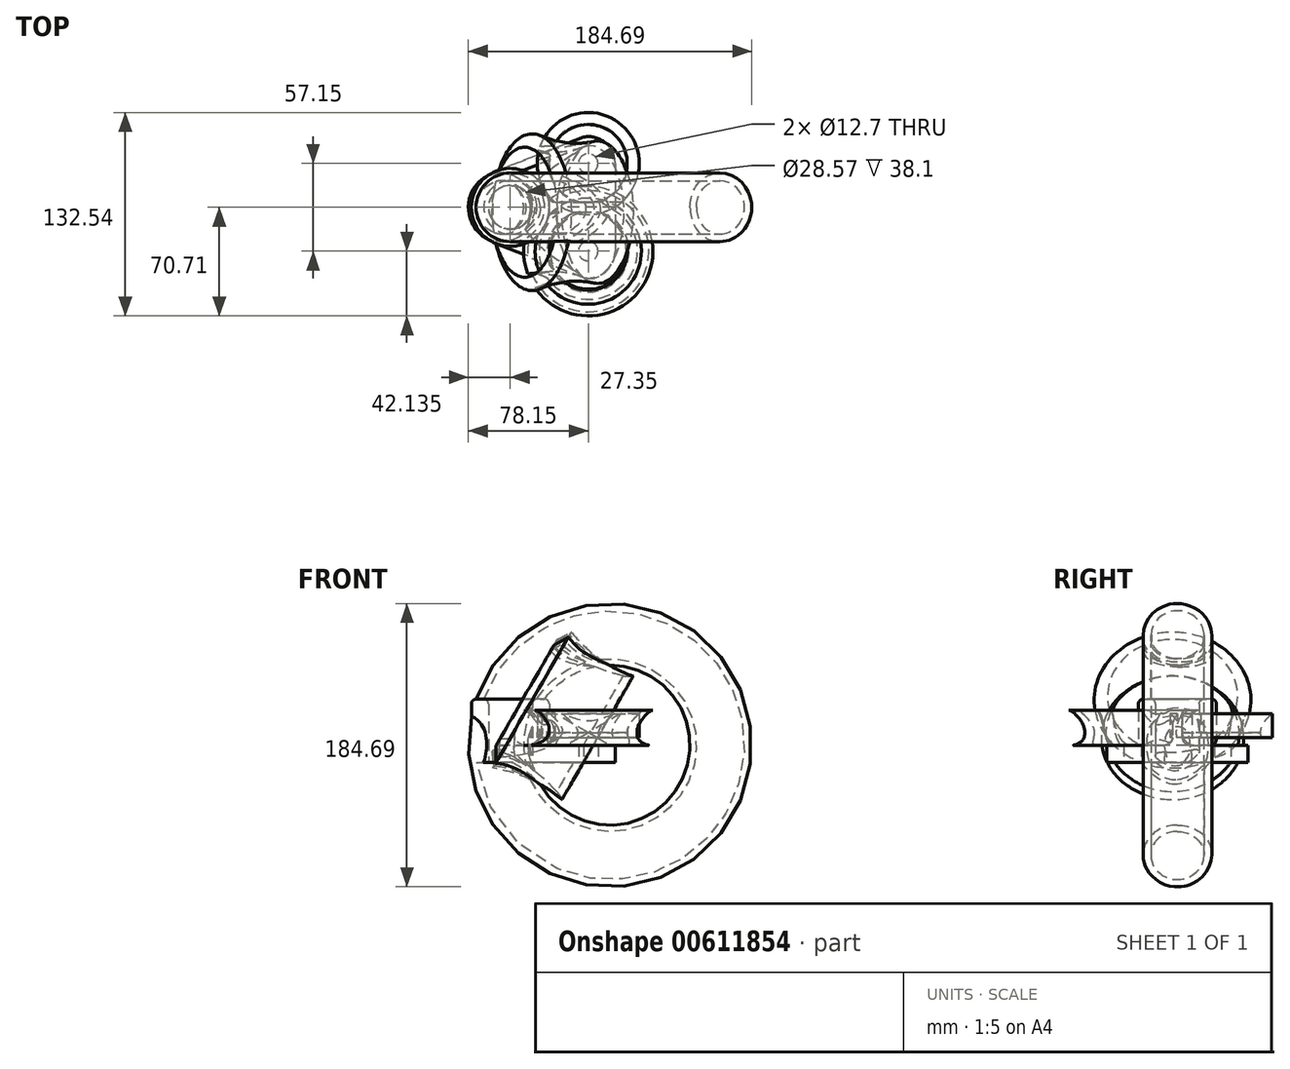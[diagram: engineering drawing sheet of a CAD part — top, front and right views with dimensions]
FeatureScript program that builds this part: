
annotation { "Feature Type Name" : "Feature", "Feature Type Description" : "" }
export const myFeature = defineFeature(function(context is Context, id is Id, definition is map)
    precondition{}
    {
        {
            var Q0;
            Q0=qCreatedBy(makeId("Top.planeOp"),FACE);
            var sketch = newSketch(context, id + "F0", { "sketchPlane" : qUnion([Q0])});
            skCircle(sketch, "E0", {"center": v(0, 0) * mm, "radius": 14.29 * mm});
            skCircle(sketch, "E1", {"center": v(0, 0) * mm, "radius": 25.4 * mm});
            skCircle(sketch, "E2", {"center": v(50.8, 28.57) * mm, "radius": 6.35 * mm});
            skCircle(sketch, "E3", {"center": v(50.8, -28.58) * mm, "radius": 6.35 * mm});
            skArc(sketch, "E4", {"start": v(47.66, 45.81) * mm, "mid": v(62.02, 42.03) * mm, "end": v(68.32, 28.57) * mm});
            skLineSegment(sketch, "E5", {"start": v(47.66, 45.81) * mm, "end": v(-9.22, 23.67) * mm});
            skLineSegment(sketch, "E6", {"start": v(68.32, 28.57) * mm, "end": v(68.32, 0) * mm});
            skLineSegment(sketch, "E7.MirrorCS", {"start": v(68.32, -28.57) * mm, "end": v(68.32, 0) * mm});
            skArc(sketch, "E8.MirrorCS", {"start": v(47.66, -45.81) * mm, "mid": v(62.02, -42.03) * mm, "end": v(68.32, -28.57) * mm});
            skLineSegment(sketch, "E9.MirrorCS", {"start": v(47.66, -45.81) * mm, "end": v(-9.22, -23.67) * mm});
            skSolve(sketch);
        }
        {
            var Q0;
            Q0=makeQuery(id+"F0.imprint","IMPRINT",FACE,{"disambiguationData":[TD([[makeQuery(id+"F0.imprint","IMPRINT",EDGE,{"derivedFrom":sQuery(id+"F0.wireOp",EDGE,"E0")}),-1.0]])]});
            extrude(context, id + "F1", {"entities" : qUnion([Q0]), "depth" : 41.15 * mm, "offsetDistance" : 25.4 * mm});
        }
        {
            var Q0;
            Q0=makeQuery(id+"F0.imprint","IMPRINT",FACE,{"disambiguationData":[TD([[makeQuery(id+"F0.imprint","IMPRINT",EDGE,{"derivedFrom":sQuery(id+"F0.wireOp",EDGE,"E2")}),-1.0]])]});
            extrude(context, id + "F2", {"entities" : qUnion([Q0]), "operationType" : NewBodyOperationType.ADD, "depth" : 11.18 * mm, "offsetDistance" : 25.4 * mm});
        }
        {
            var Q0;
            Q0=qCreatedBy(makeId("Front.planeOp"),FACE);
            var sketch = newSketch(context, id + "F3", { "sketchPlane" : qUnion([Q0])});
            skLineSegment(sketch, "E10", {"start": v(25.4, 11.16) * mm, "end": v(65.02, 11.16) * mm});
            skLineSegment(sketch, "E11", {"start": v(65.02, 11.16) * mm, "end": v(25.4, 34.04) * mm});
            skPoint(sketch, "E12.orphan", {"position": v(25.4, 41.15) * mm});
            skLineSegment(sketch, "E13", {"start": v(25.4, 11.16) * mm, "end": v(19.95, 11.16) * mm});
            skLineSegment(sketch, "E14", {"start": v(19.95, 11.16) * mm, "end": v(19.95, 35.74) * mm});
            skLineSegment(sketch, "E15", {"start": v(19.95, 35.74) * mm, "end": v(25.4, 34.04) * mm});
            skSolve(sketch);
        }
        {
            var Q0;
            Q0=makeQuery(id+"F3.imprint","IMPRINT",FACE,{"disambiguationData":[TD([[makeQuery(id+"F3.imprint","IMPRINT",EDGE,{"derivedFrom":sQuery(id+"F3.wireOp",EDGE,"E10")}),1.0]])]});
            extrude(context, id + "F4", {"entities" : qUnion([Q0]), "operationType" : NewBodyOperationType.ADD, "endBound" : BoundingType.SYMMETRIC, "depth" : 6.35 * mm, "offsetDistance" : 25.4 * mm});
        }
        {
            var Q0;
            Q0=makeQuery(id+"F1.opExtrude","CAP_EDGE",EDGE,{"disambiguationData":[OSD([sQuery(id+"F0.wireOp",EDGE,"E1")])],"isStart":false});
            var Q1;
            Q1=makeQuery(id+"F1.opExtrude","CAP_EDGE",EDGE,{"disambiguationData":[OSD([sQuery(id+"F0.wireOp",EDGE,"E0")])],"isStart":false});
            fillet(context, id + "F5", {"entities" : qUnion([Q0, Q1]), "radius" : 3.05 * mm, "tangentPropagation" : true, "allowEdgeOverflow" : false});
        }
        {
            var Q0;
            {var subQ0=sQuery(id+"F0.wireOp",EDGE,"E1");var subQ1=sQuery(id+"F0.wireOp",EDGE,"E9.MirrorCS");Q0=makeQuery(id+"F4.boolean.opBoolean","SPLIT",EDGE,{"disambiguationData":[TD([makeQuery(id+"F2.opExtrude","SWEPT_FACE",FACE,{"disambiguationData":[OSD([subQ1])]})])],"derivedFrom":makeQuery(id+"F2.opExtrude","CAP_EDGE",EDGE,{"disambiguationData":[OSD([subQ0])],"isStart":false})});}
            var Q1;
            {var subQ0=sQuery(id+"F0.wireOp",EDGE,"E1");var subQ1=sQuery(id+"F0.wireOp",EDGE,"E5");Q1=makeQuery(id+"F4.boolean.opBoolean","SPLIT",EDGE,{"disambiguationData":[TD([makeQuery(id+"F2.opExtrude","SWEPT_FACE",FACE,{"disambiguationData":[OSD([subQ1])]})])],"derivedFrom":makeQuery(id+"F2.opExtrude","CAP_EDGE",EDGE,{"disambiguationData":[OSD([subQ0])],"isStart":false})});}
            var Q2;
            Q2=makeQuery(id+"F4.boolean.opBoolean","INTERSECT",EDGE,{"derivedFrom":[makeQuery(id+"F1.opExtrude","SWEPT_FACE",FACE,{"disambiguationData":[OSD([sQuery(id+"F0.wireOp",EDGE,"E1")])]}),makeQuery(id+"F4.opExtrude","CAP_FACE",FACE,{"disambiguationData":[OSD([sQuery(id+"F3.wireOp",EDGE,"E10"),sQuery(id+"F3.wireOp",EDGE,"E11"),sQuery(id+"F3.wireOp",EDGE,"E13"),sQuery(id+"F3.wireOp",EDGE,"E14"),sQuery(id+"F3.wireOp",EDGE,"E15")])],"isStart":false})]});
            var Q3;
            Q3=makeQuery(id+"F4.boolean.opBoolean","INTERSECT",EDGE,{"derivedFrom":[makeQuery(id+"F2.opExtrude","CAP_FACE",FACE,{"disambiguationData":[OSD([sQuery(id+"F0.wireOp",EDGE,"E1"),sQuery(id+"F0.wireOp",EDGE,"E2"),sQuery(id+"F0.wireOp",EDGE,"E3"),sQuery(id+"F0.wireOp",EDGE,"E4"),sQuery(id+"F0.wireOp",EDGE,"E5"),sQuery(id+"F0.wireOp",EDGE,"E6"),sQuery(id+"F0.wireOp",EDGE,"E7.MirrorCS"),sQuery(id+"F0.wireOp",EDGE,"E8.MirrorCS"),sQuery(id+"F0.wireOp",EDGE,"E9.MirrorCS")])],"isStart":false}),makeQuery(id+"F4.opExtrude","CAP_FACE",FACE,{"disambiguationData":[OSD([sQuery(id+"F3.wireOp",EDGE,"E10"),sQuery(id+"F3.wireOp",EDGE,"E11"),sQuery(id+"F3.wireOp",EDGE,"E13"),sQuery(id+"F3.wireOp",EDGE,"E14"),sQuery(id+"F3.wireOp",EDGE,"E15")])],"isStart":false})]});
            var Q4;
            Q4=makeQuery(id+"F4.boolean.opBoolean","INTERSECT",EDGE,{"derivedFrom":[makeQuery(id+"F2.opExtrude","CAP_FACE",FACE,{"disambiguationData":[OSD([sQuery(id+"F0.wireOp",EDGE,"E1"),sQuery(id+"F0.wireOp",EDGE,"E2"),sQuery(id+"F0.wireOp",EDGE,"E3"),sQuery(id+"F0.wireOp",EDGE,"E4"),sQuery(id+"F0.wireOp",EDGE,"E5"),sQuery(id+"F0.wireOp",EDGE,"E6"),sQuery(id+"F0.wireOp",EDGE,"E7.MirrorCS"),sQuery(id+"F0.wireOp",EDGE,"E8.MirrorCS"),sQuery(id+"F0.wireOp",EDGE,"E9.MirrorCS")])],"isStart":false}),makeQuery(id+"F4.opExtrude","CAP_FACE",FACE,{"disambiguationData":[OSD([sQuery(id+"F3.wireOp",EDGE,"E10"),sQuery(id+"F3.wireOp",EDGE,"E11"),sQuery(id+"F3.wireOp",EDGE,"E13"),sQuery(id+"F3.wireOp",EDGE,"E14"),sQuery(id+"F3.wireOp",EDGE,"E15")])],"isStart":true})]});
            var Q5;
            Q5=makeQuery(id+"F4.boolean.opBoolean","INTERSECT",EDGE,{"derivedFrom":[makeQuery(id+"F1.opExtrude","SWEPT_FACE",FACE,{"disambiguationData":[OSD([sQuery(id+"F0.wireOp",EDGE,"E1")])]}),makeQuery(id+"F4.opExtrude","CAP_FACE",FACE,{"disambiguationData":[OSD([sQuery(id+"F3.wireOp",EDGE,"E10"),sQuery(id+"F3.wireOp",EDGE,"E11"),sQuery(id+"F3.wireOp",EDGE,"E13"),sQuery(id+"F3.wireOp",EDGE,"E14"),sQuery(id+"F3.wireOp",EDGE,"E15")])],"isStart":true})]});
            fillet(context, id + "F6", {"entities" : qUnion([Q0, Q1, Q2, Q3, Q4, Q5]), "radius" : 5.08 * mm, "tangentPropagation" : true, "allowEdgeOverflow" : false});
        }
        {
            var Q0;
            Q0=makeQuery(id+"F2.opExtrude","SWEPT_FACE",FACE,{"disambiguationData":[OSD([sQuery(id+"F0.wireOp",EDGE,"E9.MirrorCS")])]});
            var Q1;
            Q1=makeQuery(id+"F4.opExtrude","CAP_EDGE",EDGE,{"disambiguationData":[OSD([sQuery(id+"F3.wireOp",EDGE,"E11")])],"isStart":false});
            revolve(context, id + "F7", {"operationType" : NewBodyOperationType.ADD, "entities" : qUnion([Q0]), "axis" : qUnion([Q1]), "revolveType" : RevolveType.FULL});
        }
        {
            var Q0;
            Q0=makeQuery(id+"F1.opExtrude","CAP_FACE",FACE,{"disambiguationData":[OSD([sQuery(id+"F0.wireOp",EDGE,"E0"),sQuery(id+"F0.wireOp",EDGE,"E1")])],"isStart":false});
            var Q1;
            Q1=makeQuery(id+"F4.boolean.opBoolean","INTERSECT",EDGE,{"derivedFrom":[makeQuery(id+"F2.opExtrude","CAP_FACE",FACE,{"disambiguationData":[OSD([sQuery(id+"F0.wireOp",EDGE,"E1"),sQuery(id+"F0.wireOp",EDGE,"E2"),sQuery(id+"F0.wireOp",EDGE,"E3"),sQuery(id+"F0.wireOp",EDGE,"E4"),sQuery(id+"F0.wireOp",EDGE,"E5"),sQuery(id+"F0.wireOp",EDGE,"E6"),sQuery(id+"F0.wireOp",EDGE,"E7.MirrorCS"),sQuery(id+"F0.wireOp",EDGE,"E8.MirrorCS"),sQuery(id+"F0.wireOp",EDGE,"E9.MirrorCS")])],"isStart":false}),makeQuery(id+"F4.opExtrude","SWEPT_FACE",FACE,{"disambiguationData":[OSD([sQuery(id+"F3.wireOp",EDGE,"E11")])]})]});
            revolve(context, id + "F8", {"operationType" : NewBodyOperationType.ADD, "entities" : qUnion([Q0]), "axis" : qUnion([Q1]), "revolveType" : RevolveType.FULL});
        }
        {
            var Q0;
            Q0=makeQuery(id+"F4.opExtrude","SWEPT_FACE",FACE,{"disambiguationData":[OSD([sQuery(id+"F3.wireOp",EDGE,"E11")])]});
            var Q1;
            Q1=makeQuery(id+"F2.opExtrude","CAP_EDGE",EDGE,{"disambiguationData":[OSD([sQuery(id+"F0.wireOp",EDGE,"E3")])],"isStart":false});
            revolve(context, id + "F9", {"operationType" : NewBodyOperationType.ADD, "entities" : qUnion([Q0]), "axis" : qUnion([Q1]), "revolveType" : RevolveType.FULL});
        }
        {
            var Q0;
            Q0=makeQuery(id+"F4.opExtrude","CAP_FACE",FACE,{"disambiguationData":[OSD([sQuery(id+"F3.wireOp",EDGE,"E10"),sQuery(id+"F3.wireOp",EDGE,"E11"),sQuery(id+"F3.wireOp",EDGE,"E13"),sQuery(id+"F3.wireOp",EDGE,"E14"),sQuery(id+"F3.wireOp",EDGE,"E15")])],"isStart":true});
            var Q1;
            Q1=makeQuery(id+"F2.opExtrude","CAP_EDGE",EDGE,{"disambiguationData":[OSD([sQuery(id+"F0.wireOp",EDGE,"E2")])],"isStart":true});
            revolve(context, id + "F10", {"operationType" : NewBodyOperationType.ADD, "entities" : qUnion([Q0]), "axis" : qUnion([Q1]), "revolveType" : RevolveType.FULL});
        }
    });
